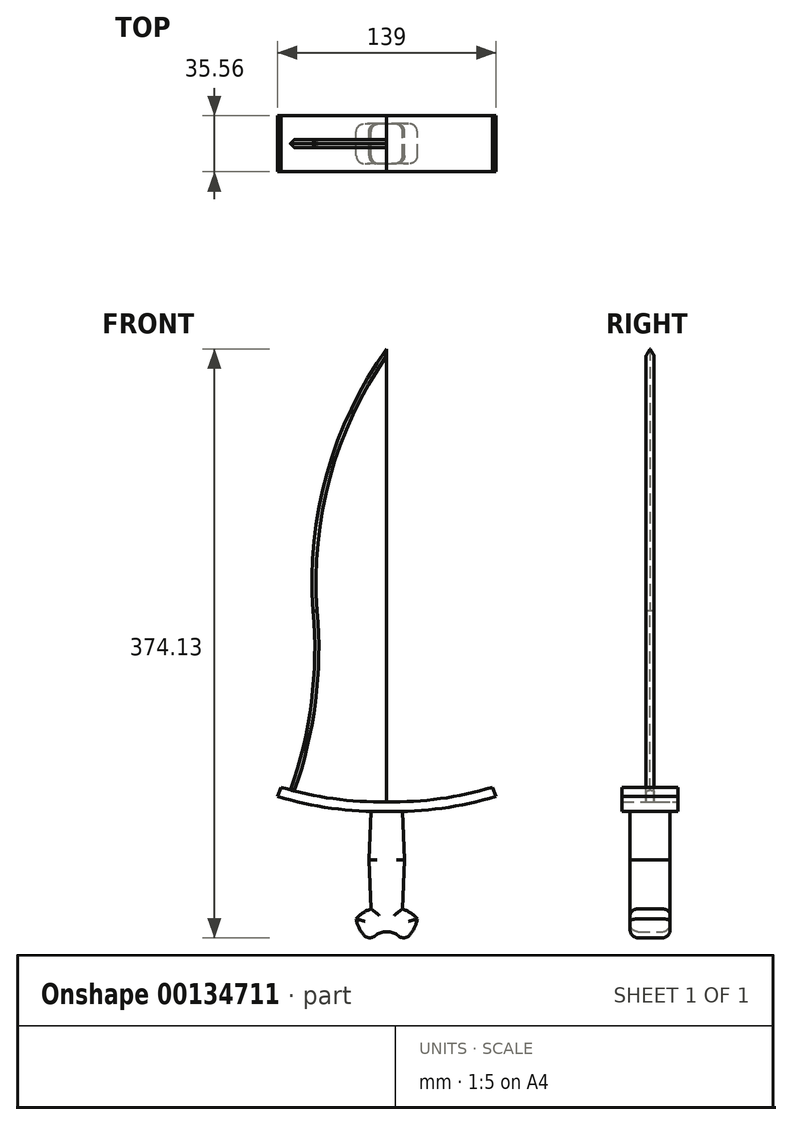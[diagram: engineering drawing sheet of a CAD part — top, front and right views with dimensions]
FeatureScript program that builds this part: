
annotation { "Feature Type Name" : "Feature", "Feature Type Description" : "" }
export const myFeature = defineFeature(function(context is Context, id is Id, definition is map)
    precondition{}
    {
        {
            var Q0;
            Q0=qCreatedBy(makeId("Front.planeOp"),FACE);
            var sketch = newSketch(context, id + "F0", { "sketchPlane" : qUnion([Q0])});
            skArc(sketch, "E0", {"start": v(10.05, -58.26) * mm, "mid": v(0, -52.47) * mm, "end": v(-10.04, -58.26) * mm});
            skArc(sketch, "E1", {"start": v(-19.38, -44.29) * mm, "mid": v(-16.28, -52.32) * mm, "end": v(-10.04, -58.26) * mm});
            skArc(sketch, "E2", {"start": v(-10.04, -38) * mm, "mid": v(-15.16, -40.48) * mm, "end": v(-19.38, -44.29) * mm});
            skArc(sketch, "E3.MirrorCS", {"start": v(19.38, -44.29) * mm, "mid": v(16.28, -52.32) * mm, "end": v(10.04, -58.26) * mm});
            skArc(sketch, "E4.MirrorCS", {"start": v(10.04, -38) * mm, "mid": v(15.16, -40.48) * mm, "end": v(19.38, -44.29) * mm});
            skLineSegment(sketch, "E5", {"start": v(-10.04, -38) * mm, "end": v(-11.4, -6.7) * mm});
            skLineSegment(sketch, "E6", {"start": v(-11.4, -6.7) * mm, "end": v(-10.04, 23.94) * mm});
            skLineSegment(sketch, "E7.MirrorCS", {"start": v(11.4, -6.7) * mm, "end": v(10.04, 23.94) * mm});
            skLineSegment(sketch, "E8.MirrorCS", {"start": v(10.04, -38) * mm, "end": v(11.4, -6.7) * mm});
            skArc(sketch, "E9", {"start": v(-69.5, 33.55) * mm, "mid": v(-35.13, 25.99) * mm, "end": v(0, 23.94) * mm});
            skArc(sketch, "E10.MirrorCS", {"start": v(69.5, 33.55) * mm, "mid": v(35.13, 25.99) * mm, "end": v(0, 23.94) * mm});
            skLineSegment(sketch, "E11", {"start": v(-69.5, 33.55) * mm, "end": v(-67.25, 39.29) * mm});
            skLineSegment(sketch, "E12.MirrorCS", {"start": v(69.5, 33.55) * mm, "end": v(67.25, 39.29) * mm});
            skArc(sketch, "E13.0", {"start": v(67.25, 39.29) * mm, "mid": v(33.99, 32.03) * mm, "end": v(0, 30.1) * mm});
            skArc(sketch, "E13.1", {"start": v(-67.25, 39.29) * mm, "mid": v(-33.99, 32.03) * mm, "end": v(0, 30.1) * mm});
            skLineSegment(sketch, "E14", {"start": v(-10.04, 23.94) * mm, "end": v(-10.03, 23.96) * mm});
            skLineSegment(sketch, "E15", {"start": v(10.04, 23.94) * mm, "end": v(10.03, 23.96) * mm});
            skArc(sketch, "E16", {"start": v(-61.25, 37.57) * mm, "mid": v(-47.8, 93.56) * mm, "end": v(-46.75, 151.13) * mm});
            skArc(sketch, "E17", {"start": v(0, 317.79) * mm, "mid": v(-38, 238.56) * mm, "end": v(-46.75, 151.13) * mm});
            skArc(sketch, "E18.MirrorCS", {"start": v(61.25, 37.57) * mm, "mid": v(47.8, 93.56) * mm, "end": v(46.75, 151.13) * mm});
            skArc(sketch, "E19.MirrorCS", {"start": v(0, 317.79) * mm, "mid": v(38, 238.56) * mm, "end": v(46.75, 151.13) * mm});
            skLineSegment(sketch, "E20", {"start": v(0, 30.1) * mm, "end": v(0, 317.79) * mm});
            skSolve(sketch);
        }
        {
            var Q0;
            {var subQ0=sQuery(id+"F0.wireOp",EDGE,"E1");Q0=makeQuery(id+"F0.imprint","IMPRINT",FACE,{"disambiguationData":[TD([[makeQuery(id+"F0.imprint","IMPRINT",EDGE,{"derivedFrom":subQ0}),1.0]])]});}
            extrude(context, id + "F1", {"entities" : qUnion([Q0]), "depth" : 12.7 * mm});
        }
        {
            var Q0;
            {var subQ10=sQuery(id+"F0.wireOp",EDGE,"E11");Q0=makeQuery(id+"F0.imprint","IMPRINT",FACE,{"disambiguationData":[TD([[makeQuery(id+"F0.imprint","IMPRINT",EDGE,{"derivedFrom":subQ10}),-1.0]])]});}
            extrude(context, id + "F2", {"entities" : qUnion([Q0]), "operationType" : NewBodyOperationType.ADD, "depth" : 17.78 * mm});
        }
        {
            var Q0;
            {var subQ0=sQuery(id+"F0.wireOp",EDGE,"E1");Q0=makeQuery(id+"F0.imprint","IMPRINT",FACE,{"disambiguationData":[TD([[makeQuery(id+"F0.imprint","IMPRINT",EDGE,{"derivedFrom":subQ0}),1.0]])]});}
            extrude(context, id + "F3", {"entities" : qUnion([Q0]), "operationType" : NewBodyOperationType.ADD, "oppositeDirection" : true, "depth" : 12.7 * mm});
        }
        {
            var Q0;
            {var subQ10=sQuery(id+"F0.wireOp",EDGE,"E11");Q0=makeQuery(id+"F0.imprint","IMPRINT",FACE,{"disambiguationData":[TD([[makeQuery(id+"F0.imprint","IMPRINT",EDGE,{"derivedFrom":subQ10}),-1.0]])]});}
            extrude(context, id + "F4", {"entities" : qUnion([Q0]), "operationType" : NewBodyOperationType.ADD, "oppositeDirection" : true, "depth" : 17.78 * mm});
        }
        {
            var Q0;
            {var subQ2=sQuery(id+"F0.wireOp",EDGE,"E18.MirrorCS");Q0=makeQuery(id+"F0.imprint","IMPRINT",FACE,{"disambiguationData":[TD([[makeQuery(id+"F0.imprint","IMPRINT",EDGE,{"derivedFrom":subQ2}),1.0]])]});}
            var Q1;
            {var subQ2=sQuery(id+"F0.wireOp",EDGE,"E16");Q1=makeQuery(id+"F0.imprint","IMPRINT",FACE,{"disambiguationData":[TD([[makeQuery(id+"F0.imprint","IMPRINT",EDGE,{"derivedFrom":subQ2}),-1.0]])]});}
            extrude(context, id + "F5", {"entities" : qUnion([Q0, Q1]), "operationType" : NewBodyOperationType.ADD, "depth" : 2.54 * mm});
        }
        {
            var Q0;
            {var subQ2=sQuery(id+"F0.wireOp",EDGE,"E18.MirrorCS");Q0=makeQuery(id+"F0.imprint","IMPRINT",FACE,{"disambiguationData":[TD([[makeQuery(id+"F0.imprint","IMPRINT",EDGE,{"derivedFrom":subQ2}),1.0]])]});}
            var Q1;
            {var subQ2=sQuery(id+"F0.wireOp",EDGE,"E16");Q1=makeQuery(id+"F0.imprint","IMPRINT",FACE,{"disambiguationData":[TD([[makeQuery(id+"F0.imprint","IMPRINT",EDGE,{"derivedFrom":subQ2}),-1.0]])]});}
            extrude(context, id + "F6", {"entities" : qUnion([Q0, Q1]), "operationType" : NewBodyOperationType.ADD, "oppositeDirection" : true, "depth" : 2.54 * mm});
        }
        {
            var Q0;
            Q0=makeQuery(id+"F1.opExtrude","CAP_EDGE",EDGE,{"disambiguationData":[OSD([sQuery(id+"F0.wireOp",EDGE,"E6")])],"isStart":false});
            var Q1;
            Q1=makeQuery(id+"F1.opExtrude","CAP_EDGE",EDGE,{"disambiguationData":[OSD([sQuery(id+"F0.wireOp",EDGE,"E5")])],"isStart":false});
            var Q2;
            Q2=makeQuery(id+"F1.opExtrude","CAP_EDGE",EDGE,{"disambiguationData":[OSD([sQuery(id+"F0.wireOp",EDGE,"E8.MirrorCS")])],"isStart":false});
            var Q3;
            Q3=makeQuery(id+"F3.opExtrude","CAP_EDGE",EDGE,{"disambiguationData":[OSD([sQuery(id+"F0.wireOp",EDGE,"E8.MirrorCS")])],"isStart":false});
            var Q4;
            Q4=makeQuery(id+"F3.opExtrude","CAP_EDGE",EDGE,{"disambiguationData":[OSD([sQuery(id+"F0.wireOp",EDGE,"E7.MirrorCS")])],"isStart":false});
            var Q5;
            Q5=makeQuery(id+"F1.opExtrude","CAP_EDGE",EDGE,{"disambiguationData":[OSD([sQuery(id+"F0.wireOp",EDGE,"E7.MirrorCS")])],"isStart":false});
            var Q6;
            Q6=makeQuery(id+"F3.opExtrude","CAP_EDGE",EDGE,{"disambiguationData":[OSD([sQuery(id+"F0.wireOp",EDGE,"E6")])],"isStart":false});
            var Q7;
            Q7=makeQuery(id+"F3.opExtrude","CAP_EDGE",EDGE,{"disambiguationData":[OSD([sQuery(id+"F0.wireOp",EDGE,"E5")])],"isStart":false});
            var Q8;
            Q8=makeQuery(id+"F3.opExtrude","CAP_EDGE",EDGE,{"disambiguationData":[OSD([sQuery(id+"F0.wireOp",EDGE,"E4.MirrorCS")])],"isStart":false});
            var Q9;
            Q9=makeQuery(id+"F3.opExtrude","CAP_EDGE",EDGE,{"disambiguationData":[OSD([sQuery(id+"F0.wireOp",EDGE,"E2")])],"isStart":false});
            var Q10;
            Q10=makeQuery(id+"F3.opExtrude","CAP_EDGE",EDGE,{"disambiguationData":[OSD([sQuery(id+"F0.wireOp",EDGE,"E3.MirrorCS")])],"isStart":false});
            var Q11;
            Q11=makeQuery(id+"F3.opExtrude","CAP_EDGE",EDGE,{"disambiguationData":[OSD([sQuery(id+"F0.wireOp",EDGE,"E0")])],"isStart":false});
            var Q12;
            Q12=makeQuery(id+"F3.opExtrude","CAP_EDGE",EDGE,{"disambiguationData":[OSD([sQuery(id+"F0.wireOp",EDGE,"E1")])],"isStart":false});
            var Q13;
            Q13=makeQuery(id+"F1.opExtrude","CAP_EDGE",EDGE,{"disambiguationData":[OSD([sQuery(id+"F0.wireOp",EDGE,"E2")])],"isStart":false});
            var Q14;
            Q14=makeQuery(id+"F1.opExtrude","CAP_EDGE",EDGE,{"disambiguationData":[OSD([sQuery(id+"F0.wireOp",EDGE,"E4.MirrorCS")])],"isStart":false});
            var Q15;
            Q15=makeQuery(id+"F1.opExtrude","CAP_EDGE",EDGE,{"disambiguationData":[OSD([sQuery(id+"F0.wireOp",EDGE,"E3.MirrorCS")])],"isStart":false});
            var Q16;
            Q16=makeQuery(id+"F1.opExtrude","CAP_EDGE",EDGE,{"disambiguationData":[OSD([sQuery(id+"F0.wireOp",EDGE,"E1")])],"isStart":false});
            var Q17;
            Q17=makeQuery(id+"F1.opExtrude","CAP_EDGE",EDGE,{"disambiguationData":[OSD([sQuery(id+"F0.wireOp",EDGE,"E0")])],"isStart":false});
            var Q18;
            {var subQ0=sQuery(id+"F0.wireOp",EDGE,"E1");var subQ1=sQuery(id+"F0.wireOp",EDGE,"E0");Q18=makeQuery(id+"F3.boolean.opBoolean","MERGE",EDGE,{"derivedFrom":[makeQuery(id+"F1.opExtrude","SWEPT_EDGE",EDGE,{"disambiguationData":[OSD([subQ1,subQ0])]}),makeQuery(id+"F3.opExtrude","SWEPT_EDGE",EDGE,{"disambiguationData":[OSD([subQ1,subQ0])]})]});}
            var Q19;
            {var subQ0=sQuery(id+"F0.wireOp",EDGE,"E3.MirrorCS");var subQ1=sQuery(id+"F0.wireOp",EDGE,"E0");Q19=makeQuery(id+"F3.boolean.opBoolean","MERGE",EDGE,{"derivedFrom":[makeQuery(id+"F1.opExtrude","SWEPT_EDGE",EDGE,{"disambiguationData":[OSD([subQ1,subQ0])]}),makeQuery(id+"F3.opExtrude","SWEPT_EDGE",EDGE,{"disambiguationData":[OSD([subQ1,subQ0])]})]});}
            fillet(context, id + "F7", {"entities" : qUnion([Q0, Q1, Q2, Q3, Q4, Q5, Q6, Q7, Q8, Q9, Q10, Q11, Q12, Q13, Q14, Q15, Q16, Q17, Q18, Q19]), "radius" : 5.08 * mm, "tangentPropagation" : true, "allowEdgeOverflow" : false});
        }
        {
            var Q0;
            Q0=makeQuery(id+"F5.opExtrude","CAP_EDGE",EDGE,{"disambiguationData":[OSD([sQuery(id+"F0.wireOp",EDGE,"E16")])],"isStart":false});
            var Q1;
            Q1=makeQuery(id+"F5.opExtrude","CAP_EDGE",EDGE,{"disambiguationData":[OSD([sQuery(id+"F0.wireOp",EDGE,"E17")])],"isStart":false});
            var Q2;
            Q2=makeQuery(id+"F5.opExtrude","CAP_EDGE",EDGE,{"disambiguationData":[OSD([sQuery(id+"F0.wireOp",EDGE,"E18.MirrorCS")])],"isStart":false});
            var Q3;
            Q3=makeQuery(id+"F5.opExtrude","CAP_EDGE",EDGE,{"disambiguationData":[OSD([sQuery(id+"F0.wireOp",EDGE,"E19.MirrorCS")])],"isStart":false});
            var Q4;
            Q4=makeQuery(id+"F6.opExtrude","CAP_EDGE",EDGE,{"disambiguationData":[OSD([sQuery(id+"F0.wireOp",EDGE,"E19.MirrorCS")])],"isStart":false});
            var Q5;
            Q5=makeQuery(id+"F6.opExtrude","CAP_EDGE",EDGE,{"disambiguationData":[OSD([sQuery(id+"F0.wireOp",EDGE,"E18.MirrorCS")])],"isStart":false});
            var Q6;
            Q6=makeQuery(id+"F6.opExtrude","CAP_EDGE",EDGE,{"disambiguationData":[OSD([sQuery(id+"F0.wireOp",EDGE,"E17")])],"isStart":false});
            var Q7;
            Q7=makeQuery(id+"F6.opExtrude","CAP_EDGE",EDGE,{"disambiguationData":[OSD([sQuery(id+"F0.wireOp",EDGE,"E16")])],"isStart":false});
            chamfer(context, id + "F8", {"entities" : qUnion([Q0, Q1, Q2, Q3, Q4, Q5, Q6, Q7]), "width" : 2.54 * mm, "tangentPropagation" : true});
        }
    });
